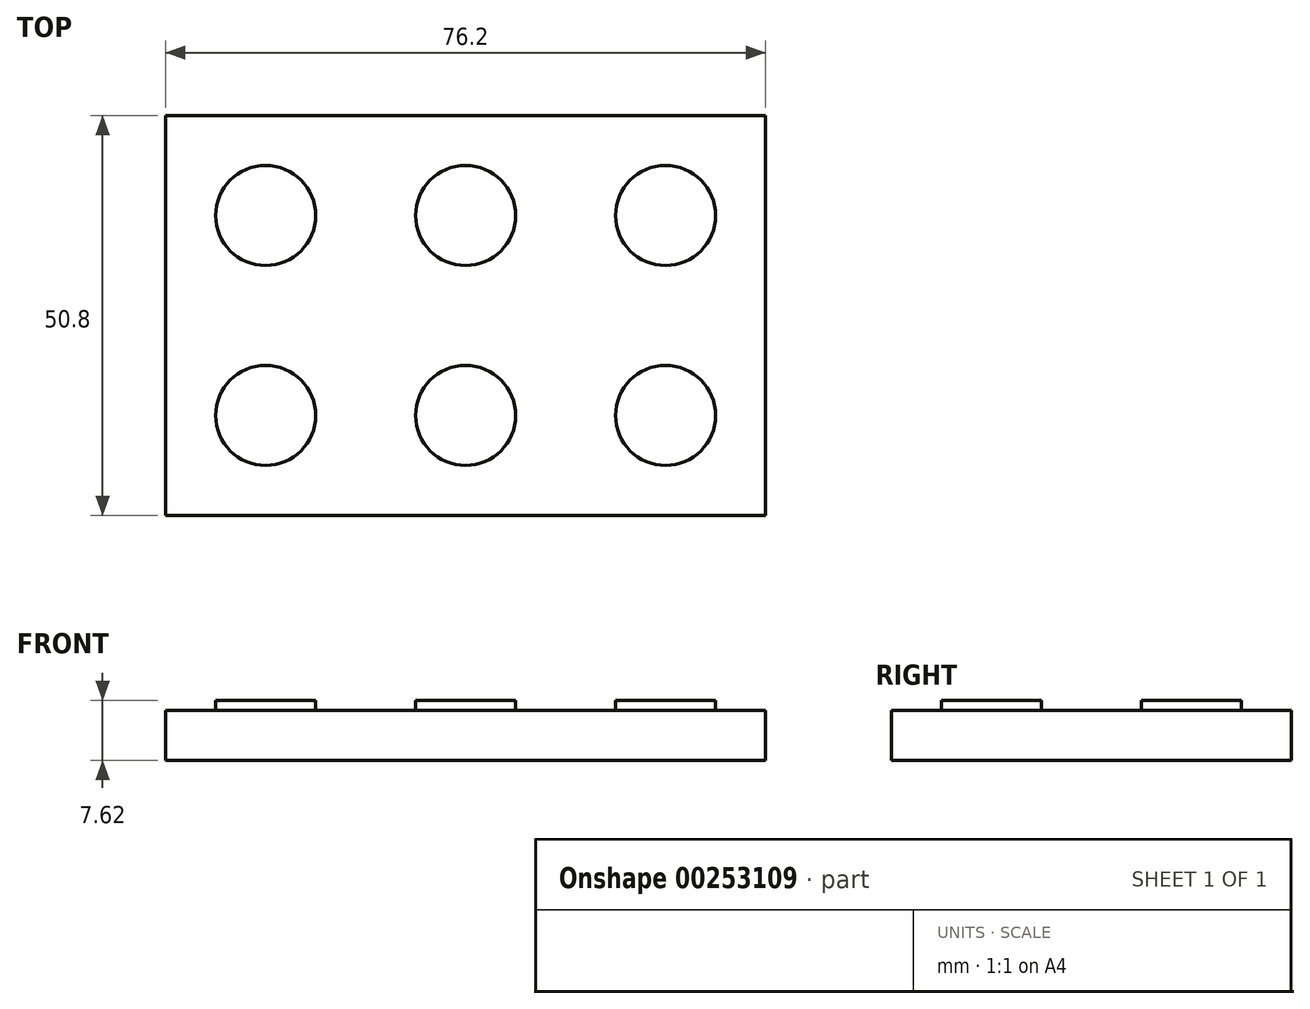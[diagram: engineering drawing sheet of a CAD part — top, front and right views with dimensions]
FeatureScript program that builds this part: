
annotation { "Feature Type Name" : "Feature", "Feature Type Description" : "" }
export const myFeature = defineFeature(function(context is Context, id is Id, definition is map)
    precondition{}
    {
        {
            var Q0;
            Q0=qCreatedBy(makeId("Top.planeOp"),FACE);
            var sketch = newSketch(context, id + "F0", { "sketchPlane" : qUnion([Q0])});
            skLineSegment(sketch, "E0.bottom", {"start": v(-41.9, 4.86) * mm, "end": v(34.3, 4.86) * mm});
            skLineSegment(sketch, "E0.top", {"start": v(-41.9, -45.94) * mm, "end": v(34.3, -45.94) * mm});
            skLineSegment(sketch, "E0.left", {"start": v(-41.9, 4.86) * mm, "end": v(-41.9, -45.94) * mm});
            skLineSegment(sketch, "E0.right", {"start": v(34.3, 4.86) * mm, "end": v(34.3, -45.94) * mm});
            skLineSegment(sketch, "E1", {"start": v(-41.9, 4.86) * mm, "end": v(-41.9, -7.84) * mm});
            skLineSegment(sketch, "E2", {"start": v(-41.9, -7.84) * mm, "end": v(-41.9, -33.24) * mm});
            skLineSegment(sketch, "E3", {"start": v(-41.9, 4.86) * mm, "end": v(-29.2, 4.86) * mm});
            skLineSegment(sketch, "E4", {"start": v(-29.2, 4.86) * mm, "end": v(-3.8, 4.86) * mm});
            skLineSegment(sketch, "E5", {"start": v(-3.8, 4.86) * mm, "end": v(21.6, 4.86) * mm});
            skCircle(sketch, "E6", {"center": v(-29.2, -7.84) * mm, "radius": 6.35 * mm});
            skCircle(sketch, "E7", {"center": v(-29.2, -33.24) * mm, "radius": 6.35 * mm});
            skCircle(sketch, "E8", {"center": v(-3.8, -7.84) * mm, "radius": 6.35 * mm});
            skCircle(sketch, "E9", {"center": v(-3.8, -33.24) * mm, "radius": 6.35 * mm});
            skCircle(sketch, "E10", {"center": v(21.6, -7.84) * mm, "radius": 6.35 * mm});
            skCircle(sketch, "E11", {"center": v(21.6, -33.24) * mm, "radius": 6.35 * mm});
            skSolve(sketch);
        }
        {
            var Q0;
            Q0 = qSketchRegion(id + "F0", true);
            extrude(context, id + "F1", {"entities" : qUnion([Q0]), "depth" : 6.35 * mm});
        }
        {
            var Q0;
            Q0=makeQuery(id+"F0.imprint","IMPRINT",FACE,{"disambiguationData":[TD([[makeQuery(id+"F0.imprint","IMPRINT",EDGE,{"derivedFrom":sQuery(id+"F0.wireOp",EDGE,"E10")}),1.0]])]});
            var Q1;
            Q1=makeQuery(id+"F0.imprint","IMPRINT",FACE,{"disambiguationData":[TD([[makeQuery(id+"F0.imprint","IMPRINT",EDGE,{"derivedFrom":sQuery(id+"F0.wireOp",EDGE,"E8")}),1.0]])]});
            var Q2;
            Q2=makeQuery(id+"F0.imprint","IMPRINT",FACE,{"disambiguationData":[TD([[makeQuery(id+"F0.imprint","IMPRINT",EDGE,{"derivedFrom":sQuery(id+"F0.wireOp",EDGE,"E6")}),1.0]])]});
            var Q3;
            Q3=makeQuery(id+"F0.imprint","IMPRINT",FACE,{"disambiguationData":[TD([[makeQuery(id+"F0.imprint","IMPRINT",EDGE,{"derivedFrom":sQuery(id+"F0.wireOp",EDGE,"E7")}),1.0]])]});
            var Q4;
            Q4=makeQuery(id+"F0.imprint","IMPRINT",FACE,{"disambiguationData":[TD([[makeQuery(id+"F0.imprint","IMPRINT",EDGE,{"derivedFrom":sQuery(id+"F0.wireOp",EDGE,"E9")}),1.0]])]});
            var Q5;
            Q5=makeQuery(id+"F0.imprint","IMPRINT",FACE,{"disambiguationData":[TD([[makeQuery(id+"F0.imprint","IMPRINT",EDGE,{"derivedFrom":sQuery(id+"F0.wireOp",EDGE,"E11")}),1.0]])]});
            extrude(context, id + "F2", {"entities" : qUnion([Q0, Q1, Q2, Q3, Q4, Q5]), "operationType" : NewBodyOperationType.ADD, "depth" : 7.62 * mm});
        }
    });
